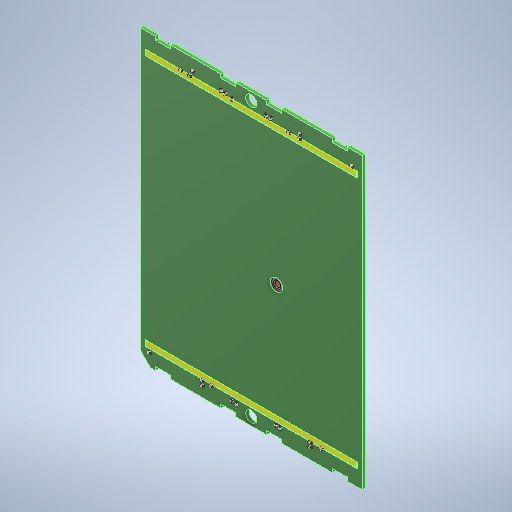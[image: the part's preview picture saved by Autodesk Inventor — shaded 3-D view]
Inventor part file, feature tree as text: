
AUTODESK INVENTOR PART (.ipt)
format: ipt  version: 2025 (Build 290162000, 162)  size: 5,618,176 bytes
history: native  units: in
note: dims shown in document units (in); Inventor stores cm internally (conversion verified against a paired STEP export)
features: other x227, extrude x1, sketch x1
ambient origin geometry x8: Origin, YZ Plane, XZ Plane, XY Plane, X Axis, Y Axis, Z Axis, Center Point
bodies: Solid1 (feature_tree), Solid2 (feature_tree), Solid3 (feature_tree), Solid4 (feature_tree), Solid5 (feature_tree), Solid6 (feature_tree), Solid7 (feature_tree), Solid8 (feature_tree), Solid9 (feature_tree), Solid10 (feature_tree), Solid11 (feature_tree), Solid12 (feature_tree), Solid13 (feature_tree), Solid14 (feature_tree), Solid15 (feature_tree), Solid16 (feature_tree), Solid17 (feature_tree), Solid18 (feature_tree), Solid19 (feature_tree), Solid20 (feature_tree), Solid21 (feature_tree), Solid22 (feature_tree), Solid23 (feature_tree), Solid24 (feature_tree), Solid25 (feature_tree), Solid26 (feature_tree), Solid27 (feature_tree), Solid28 (feature_tree), Solid29 (feature_tree), Solid30 (feature_tree), Solid31 (feature_tree), Solid32 (feature_tree), Solid33 (feature_tree), Solid34 (feature_tree), Solid35 (feature_tree), Solid36 (feature_tree), Solid37 (feature_tree), Solid38 (feature_tree), Solid39 (feature_tree), Solid40 (feature_tree), Solid41 (feature_tree), Solid42 (feature_tree), Solid43 (feature_tree), Solid44 (feature_tree), Solid45 (feature_tree), Solid46 (feature_tree), Solid47 (feature_tree), Solid48 (feature_tree), Solid49 (feature_tree), Solid50 (feature_tree), Solid51 (feature_tree), Solid52 (feature_tree), Solid53 (feature_tree), Solid54 (feature_tree), Solid55 (feature_tree), Solid56 (feature_tree), Solid57 (feature_tree), Solid58 (feature_tree), Solid59 (feature_tree), Solid60 (feature_tree), Solid61 (feature_tree), Solid62 (feature_tree), Solid63 (feature_tree), Solid64 (feature_tree), Solid65 (feature_tree), Solid66 (feature_tree), Solid67 (feature_tree), Solid68 (feature_tree), Solid69 (feature_tree), Solid70 (feature_tree), Solid71 (feature_tree), Solid72 (feature_tree), Solid73 (feature_tree), Solid74 (feature_tree), Solid75 (feature_tree), Solid76 (feature_tree), Solid77 (feature_tree), Solid78 (feature_tree), Solid79 (feature_tree), Solid80 (feature_tree), Solid81 (feature_tree), Solid82 (feature_tree), Solid83 (feature_tree), Solid84 (feature_tree), Solid85 (feature_tree), Solid86 (feature_tree), Solid87 (feature_tree), Solid88 (feature_tree), Solid89 (feature_tree), Solid90 (feature_tree), Solid91 (feature_tree), Solid92 (feature_tree), Solid93 (feature_tree), Solid94 (feature_tree), Solid95 (feature_tree), Solid96 (feature_tree), Solid97 (feature_tree), Solid98 (feature_tree), Solid99 (feature_tree), Solid100 (feature_tree), Solid101 (feature_tree), Solid102 (feature_tree), Solid103 (feature_tree), Solid104 (feature_tree), Solid105 (feature_tree), Solid106 (feature_tree), Solid107 (feature_tree), Solid108 (feature_tree), Solid109 (feature_tree), Solid110 (feature_tree), Solid111 (feature_tree), Solid112 (feature_tree), Solid113 (feature_tree), Solid114 (feature_tree), Solid115 (feature_tree), Solid116 (feature_tree), Solid117 (feature_tree), Solid118 (feature_tree), Solid119 (feature_tree), Solid120 (feature_tree), Solid121 (feature_tree), Solid122 (feature_tree), Solid123 (feature_tree), Solid124 (feature_tree), Solid125 (feature_tree), Solid126 (feature_tree), Solid127 (feature_tree), Solid128 (feature_tree), Solid129 (feature_tree), Solid130 (feature_tree), Solid131 (feature_tree), Solid132 (feature_tree), Solid133 (feature_tree), Solid134 (feature_tree), Solid135 (feature_tree), Solid136 (feature_tree), Solid137 (feature_tree), Solid138 (feature_tree), Solid139 (feature_tree), Solid140 (feature_tree), Solid141 (feature_tree), Solid142 (feature_tree), Solid143 (feature_tree), Solid144 (feature_tree), Solid145 (feature_tree), Solid146 (feature_tree), Solid147 (feature_tree), Solid148 (feature_tree), Solid149 (feature_tree), Solid150 (feature_tree), Solid151 (feature_tree), Solid152 (feature_tree), Solid153 (feature_tree), Solid154 (feature_tree), Solid155 (feature_tree), Solid156 (feature_tree), Solid157 (feature_tree), Solid158 (feature_tree), Solid159 (feature_tree), Solid160 (feature_tree), Solid161 (feature_tree), Solid162 (feature_tree), Solid163 (feature_tree), Solid164 (feature_tree), Solid165 (feature_tree), Solid166 (feature_tree), Solid167 (feature_tree), Solid168 (feature_tree), Solid169 (feature_tree), Solid170 (feature_tree), Solid171 (feature_tree), Solid172 (feature_tree), Solid173 (feature_tree), Solid174 (feature_tree), Solid175 (feature_tree), Solid176 (feature_tree), Solid177 (feature_tree), Solid178 (feature_tree), Solid179 (feature_tree), Solid180 (feature_tree), Solid181 (feature_tree), Solid182 (feature_tree), Solid183 (feature_tree), Solid184 (feature_tree), Solid185 (feature_tree), Solid186 (feature_tree), Solid187 (feature_tree), Solid188 (feature_tree), Solid189 (feature_tree), Solid190 (feature_tree), Solid191 (feature_tree), Solid192 (feature_tree), Solid193 (feature_tree), Solid194 (feature_tree), Solid195 (feature_tree), Solid196 (feature_tree), Solid197 (feature_tree), Solid198 (feature_tree), Solid199 (feature_tree), Solid200 (feature_tree), Solid201 (feature_tree), Solid202 (feature_tree), Solid203 (feature_tree), Solid204 (feature_tree), Solid205 (feature_tree), Solid206 (feature_tree), Solid207 (feature_tree), Solid208 (feature_tree), Solid209 (feature_tree), Solid210 (feature_tree), Solid211 (feature_tree), Solid212 (feature_tree), Solid213 (feature_tree), Solid214 (feature_tree), Solid215 (feature_tree), Solid216 (feature_tree), Solid217 (feature_tree), Solid218 (feature_tree), Solid219 (feature_tree), Solid220 (feature_tree), Solid221 (feature_tree), Solid222 (feature_tree), Solid223 (feature_tree), Solid224 (feature_tree), Solid225 (feature_tree), Solid226 (feature_tree), Solid227 (feature_tree), Solid228 (feature_tree), Solid229 (feature_tree), Solid230 (feature_tree), Solid231 (feature_tree), Solid232 (feature_tree), Solid233 (feature_tree)
feature tree (229):
  extrude  "Extrusion1"  Depth=0.002in
  sketch  "Sketch1"  dims[d0=0.126in d1=0.1693in d2=0.0394in d3=0.0394in d4=0.126in d5=0.1693in d6=0.002in d7=0.0in]
  other  "Open CASCADE STEP translator 7.5 1.1.1_1:1"
  other  "CAPC0603X33N_11:1"
  other  "CAPC0603X33N_11:2"
  other  "CAPC0603X33N_11:3"
  other  "CAPC0603X33N_13:1"
  other  "CAPC0603X33N_13:2"
  other  "CAPC0603X33N_13:3"
  other  "RESC0603X28N_15:1"
  other  "RESC0603X28N_15:2"
  other  "RESC0603X28N_15:3"
  other  "SMTSO-080-2ET-PennEngineering-3D-03-15-2023_21:1"
  other  "RESC0603X28N_23:1"
  other  "RESC0603X28N_23:2"
  other  "RESC0603X28N_23:3"
  other  "RESC0603X28N_25:1"
  other  "RESC0603X28N_25:2"
  other  "RESC0603X28N_25:3"
  other  "CAPC0603X33N_27:1"
  other  "CAPC0603X33N_27:2"
  other  "CAPC0603X33N_27:3"
  other  "CAPC0603X33N_29:1"
  other  "CAPC0603X33N_29:2"
  other  "CAPC0603X33N_29:3"
  other  "RESC0603X28N_31:1"
  other  "RESC0603X28N_31:2"
  other  "RESC0603X28N_31:3"
  other  "RESC0603X28N_33:1"
  other  "RESC0603X28N_33:2"
  other  "RESC0603X28N_33:3"
  other  "RESC0603X28N_35:1"
  other  "RESC0603X28N_35:2"
  other  "RESC0603X28N_35:3"
  other  "RESC0603X28N_37:1"
  other  "RESC0603X28N_37:2"
  other  "RESC0603X28N_37:3"
  other  "RESC0603X28N_39:1"
  other  "RESC0603X28N_39:2"
  other  "RESC0603X28N_39:3"
  other  "RESC0603X28N_41:1"
  other  "RESC0603X28N_41:2"
  other  "RESC0603X28N_41:3"
  other  "RESC0603X28N_43:1"
  other  "RESC0603X28N_43:2"
  other  "RESC0603X28N_43:3"
  other  "RESC0603X28N_45:1"
  other  "RESC0603X28N_45:2"
  other  "RESC0603X28N_45:3"
  other  "RESC0603X28N_47:1"
  other  "RESC0603X28N_47:2"
  other  "RESC0603X28N_47:3"
  other  "CAPC0603X33N_49:1"
  other  "CAPC0603X33N_49:2"
  other  "CAPC0603X33N_49:3"
  other  "CAPC0603X33N_51:1"
  other  "CAPC0603X33N_51:2"
  other  "CAPC0603X33N_51:3"
  other  "CAPC0603X33N_53:1"
  other  "CAPC0603X33N_53:2"
  other  "CAPC0603X33N_53:3"
  other  "CAPC0603X33N_55:1"
  other  "CAPC0603X33N_55:2"
  other  "CAPC0603X33N_55:3"
  other  "CAPC0603X33N_57:1"
  other  "CAPC0603X33N_57:2"
  other  "CAPC0603X33N_57:3"
  other  "CAPC0603X33N_59:1"
  other  "CAPC0603X33N_59:2"
  other  "CAPC0603X33N_59:3"
  other  "CAPC0603X33N_61:1"
  other  "CAPC0603X33N_61:2"
  other  "CAPC0603X33N_61:3"
  other  "CAPC0603X33N_63:1"
  other  "CAPC0603X33N_63:2"
  other  "CAPC0603X33N_63:3"
  other  "CAPC0603X33N_65:1"
  other  "CAPC0603X33N_65:2"
  other  "CAPC0603X33N_65:3"
  other  "CAPC0603X33N_67:1"
  other  "CAPC0603X33N_67:2"
  other  "CAPC0603X33N_67:3"
  other  "CAPC0603X33N_69:1"
  other  "CAPC0603X33N_69:2"
  other  "CAPC0603X33N_69:3"
  other  "CAPC0603X33N_71:1"
  other  "CAPC0603X33N_71:2"
  other  "CAPC0603X33N_71:3"
  other  "CAPC0603X33N_73:1"
  other  "CAPC0603X33N_73:2"
  other  "CAPC0603X33N_73:3"
  other  "CAPC0603X33N_75:1"
  other  "CAPC0603X33N_75:2"
  other  "CAPC0603X33N_75:3"
  other  "CAPC0603X33N_77:1"
  other  "CAPC0603X33N_77:2"
  other  "CAPC0603X33N_77:3"
  other  "CAPC0603X33N_79:1"
  other  "CAPC0603X33N_79:2"
  other  "CAPC0603X33N_79:3"
  other  "CAPC0603X33N_81:1"
  other  "CAPC0603X33N_81:2"
  other  "CAPC0603X33N_81:3"
  other  "CAPC0603X33N_83:1"
  other  "CAPC0603X33N_83:2"
  other  "CAPC0603X33N_83:3"
  other  "CAPC0603X33N_85:1"
  other  "CAPC0603X33N_85:2"
  other  "CAPC0603X33N_85:3"
  other  "CAPC0603X33N_87:1"
  other  "CAPC0603X33N_87:2"
  other  "CAPC0603X33N_87:3"
  other  "CAPC0603X33N_89:1"
  other  "CAPC0603X33N_89:2"
  other  "CAPC0603X33N_89:3"
  other  "CAPC0603X33N_91:1"
  other  "CAPC0603X33N_91:2"
  other  "CAPC0603X33N_91:3"
  other  "CAPC0603X33N_93:1"
  other  "CAPC0603X33N_93:2"
  other  "CAPC0603X33N_93:3"
  other  "CAPC0603X33N_95:1"
  other  "CAPC0603X33N_95:2"
  other  "CAPC0603X33N_95:3"
  other  "CAPC0603X33N_97:1"
  other  "CAPC0603X33N_97:2"
  other  "CAPC0603X33N_97:3"
  other  "CAPC0603X33N_99:1"
  other  "CAPC0603X33N_99:2"
  other  "CAPC0603X33N_99:3"
  other  "CAPC1005X55N_101:1"
  other  "CAPC1005X55N_101:2"
  other  "CAPC1005X55N_101:3"
  other  "CAPC1005X55N_103:1"
  other  "CAPC1005X55N_103:2"
  other  "CAPC1005X55N_103:3"
  other  "CAPC1005X55N_105:1"
  other  "CAPC1005X55N_105:2"
  other  "CAPC1005X55N_105:3"
  other  "CAPC1005X55N_107:1"
  other  "CAPC1005X55N_107:2"
  other  "CAPC1005X55N_107:3"
  other  "CAPC0603X33N_109:1"
  other  "CAPC0603X33N_109:2"
  other  "CAPC0603X33N_109:3"
  other  "CAPC0603X33N_111:1"
  other  "CAPC0603X33N_111:2"
  other  "CAPC0603X33N_111:3"
  other  "CAPC0603X33N_113:1"
  other  "CAPC0603X33N_113:2"
  other  "CAPC0603X33N_113:3"
  other  "CAPC0603X33N_115:1"
  other  "CAPC0603X33N_115:2"
  other  "CAPC0603X33N_115:3"
  other  "CAPC0603X33N_117:1"
  other  "CAPC0603X33N_117:2"
  other  "CAPC0603X33N_117:3"
  other  "CAPC0603X33N_119:1"
  other  "CAPC0603X33N_119:2"
  other  "CAPC0603X33N_119:3"
  other  "CAPC0603X33N_121:1"
  other  "CAPC0603X33N_121:2"
  other  "CAPC0603X33N_121:3"
  other  "CAPC0603X33N_123:1"
  other  "CAPC0603X33N_123:2"
  other  "CAPC0603X33N_123:3"
  other  "CAPC0603X33N_125:1"
  other  "CAPC0603X33N_125:2"
  other  "CAPC0603X33N_125:3"
  other  "CAPC0603X33N_127:1"
  other  "CAPC0603X33N_127:2"
  other  "CAPC0603X33N_127:3"
  other  "CAPC0603X33N_129:1"
  other  "CAPC0603X33N_129:2"
  other  "CAPC0603X33N_129:3"
  other  "CAPC0603X33N_131:1"
  other  "CAPC0603X33N_131:2"
  other  "CAPC0603X33N_131:3"
  other  "CAPC0603X33N_133:1"
  other  "CAPC0603X33N_133:2"
  other  "CAPC0603X33N_133:3"
  other  "CAPC0603X33N_135:1"
  other  "CAPC0603X33N_135:2"
  other  "CAPC0603X33N_135:3"
  other  "CAPC0603X33N_137:1"
  other  "CAPC0603X33N_137:2"
  other  "CAPC0603X33N_137:3"
  other  "CAPC0603X33N_139:1"
  other  "CAPC0603X33N_139:2"
  other  "CAPC0603X33N_139:3"
  other  "CAPC0603X33N_141:1"
  other  "CAPC0603X33N_141:2"
  other  "CAPC0603X33N_141:3"
  other  "CAPC0603X33N_143:1"
  other  "CAPC0603X33N_143:2"
  other  "CAPC0603X33N_143:3"
  other  "CAPC0603X33N_145:1"
  other  "CAPC0603X33N_145:2"
  other  "CAPC0603X33N_145:3"
  other  "CAPC0603X33N_147:1"
  other  "CAPC0603X33N_147:2"
  other  "CAPC0603X33N_147:3"
  other  "CAPC0603X33N_149:1"
  other  "CAPC0603X33N_149:2"
  other  "CAPC0603X33N_149:3"
  other  "CAPC0603X33N_151:1"
  other  "CAPC0603X33N_151:2"
  other  "CAPC0603X33N_151:3"
  other  "CAPC0603X33N_153:1"
  other  "CAPC0603X33N_153:2"
  other  "CAPC0603X33N_153:3"
  other  "CAPC0603X33N_155:1"
  other  "CAPC0603X33N_155:2"
  other  "CAPC0603X33N_155:3"
  other  "CAPC0603X33N_157:1"
  other  "CAPC0603X33N_157:2"
  other  "CAPC0603X33N_157:3"
  other  "CAPC1005X55N_159:1"
  other  "CAPC1005X55N_159:2"
  other  "CAPC1005X55N_159:3"
  other  "CAPC1005X55N_161:1"
  other  "CAPC1005X55N_161:2"
  other  "CAPC1005X55N_161:3"
  other  "CAPC1005X55N_163:1"
  other  "CAPC1005X55N_163:2"
  other  "CAPC1005X55N_163:3"
  other  "CAPC1005X55N_165:1"
  other  "CAPC1005X55N_165:2"
  other  "CAPC1005X55N_165:3"
